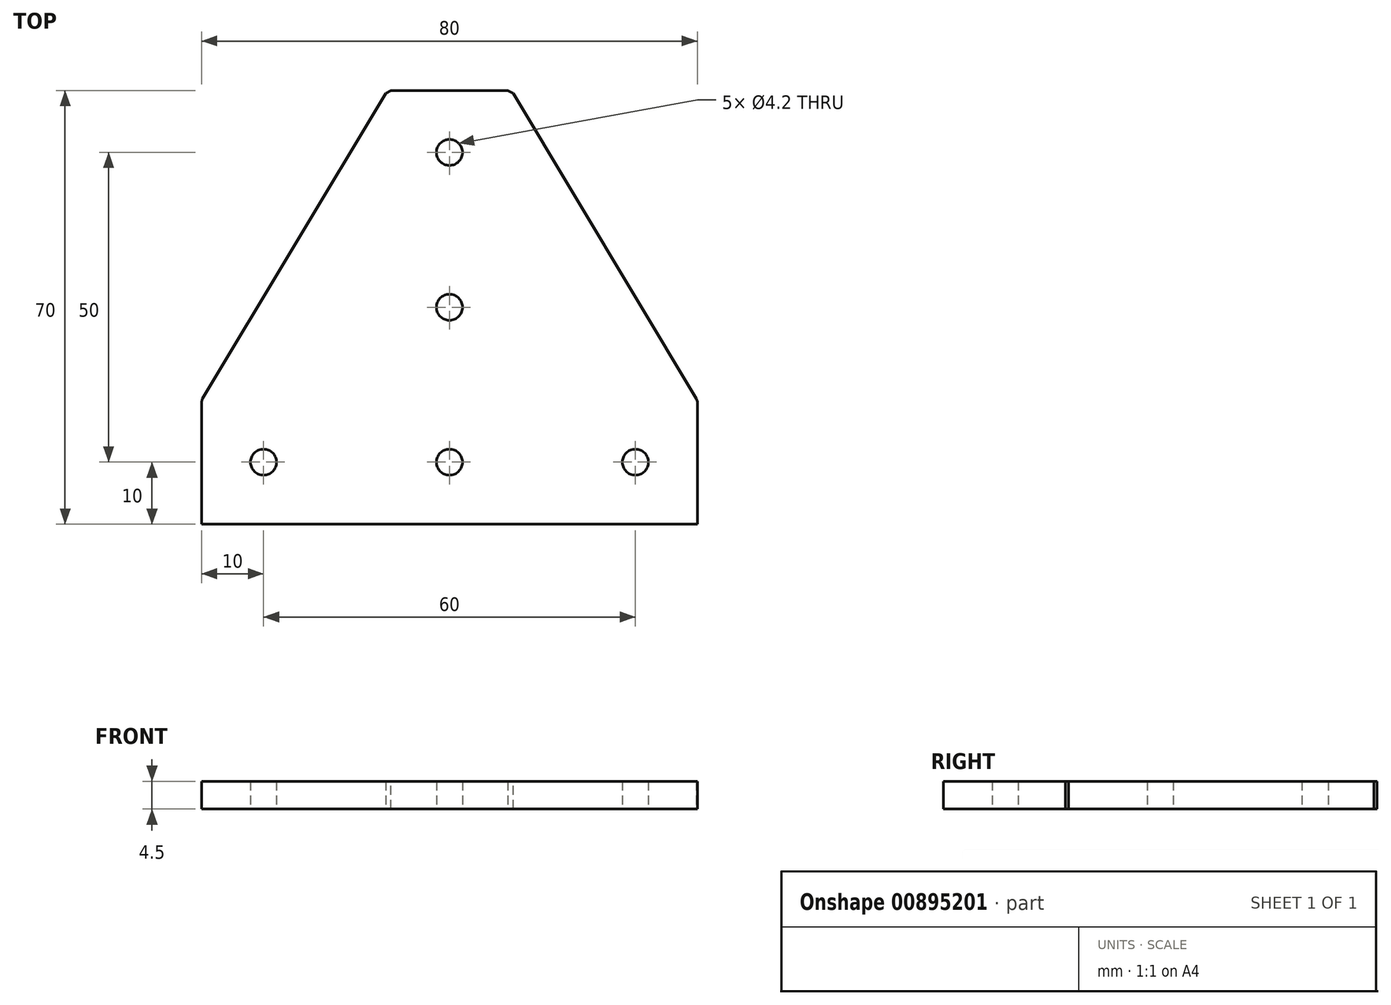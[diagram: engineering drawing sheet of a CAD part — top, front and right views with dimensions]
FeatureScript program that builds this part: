
annotation { "Feature Type Name" : "Feature", "Feature Type Description" : "" }
export const myFeature = defineFeature(function(context is Context, id is Id, definition is map)
    precondition{}
    {
        {
            var Q0;
            Q0=qCreatedBy(makeId("Top.planeOp"),FACE);
            var sketch = newSketch(context, id + "F0", { "sketchPlane" : qUnion([Q0])});
            skLineSegment(sketch, "E0", {"start": v(0, 0) * mm, "end": v(40, 0) * mm});
            skLineSegment(sketch, "E1", {"start": v(40, 0) * mm, "end": v(40, 20) * mm});
            skLineSegment(sketch, "E2.0", {"start": v(0, 60) * mm, "end": v(40, 60) * mm, "construction": true});
            skLineSegment(sketch, "E3", {"start": v(0, 60) * mm, "end": v(0, -24.18) * mm, "construction": true});
            skLineSegment(sketch, "E4.0", {"start": v(-10, 60) * mm, "end": v(-10, -24.18) * mm, "construction": true});
            skLineSegment(sketch, "E5.0", {"start": v(10, 70) * mm, "end": v(10, -24.18) * mm, "construction": true});
            skLineSegment(sketch, "E6.MirrorCS", {"start": v(0, 60) * mm, "end": v(-40, 60) * mm});
            skLineSegment(sketch, "E7.MirrorCS", {"start": v(-40, 0) * mm, "end": v(-40, 20) * mm});
            skLineSegment(sketch, "E8.MirrorCS", {"start": v(0, 0) * mm, "end": v(-40, 0) * mm});
            skLineSegment(sketch, "E9.0", {"start": v(40, 10) * mm, "end": v(-40, 10) * mm, "construction": true});
            skLineSegment(sketch, "E10.0", {"start": v(0, 70) * mm, "end": v(10, 70) * mm});
            skLineSegment(sketch, "E11.MirrorCS", {"start": v(-10, 70) * mm, "end": v(-10, -24.18) * mm, "construction": true});
            skLineSegment(sketch, "E12.MirrorCS", {"start": v(0, 70) * mm, "end": v(-10, 70) * mm});
            skLineSegment(sketch, "E13", {"start": v(-10, 70) * mm, "end": v(-40, 20) * mm});
            skLineSegment(sketch, "E14", {"start": v(10, 70) * mm, "end": v(40, 20) * mm});
            skPoint(sketch, "E15.orphan", {"position": v(40, 70) * mm});
            skPoint(sketch, "E16.orphan", {"position": v(-40, 70) * mm});
            skLineSegment(sketch, "E17.0", {"start": v(-30, 60) * mm, "end": v(-30, -24.18) * mm, "construction": true});
            skLineSegment(sketch, "E18.0", {"start": v(30, 60) * mm, "end": v(30, -24.18) * mm, "construction": true});
            skLineSegment(sketch, "E19.0", {"start": v(40, 35) * mm, "end": v(-40, 35) * mm, "construction": true});
            skLineSegment(sketch, "E20.0", {"start": v(40, 60) * mm, "end": v(-40, 60) * mm, "construction": true});
            skCircle(sketch, "E21", {"center": v(0, 60) * mm, "radius": 2.1 * mm});
            skCircle(sketch, "E22", {"center": v(0, 35) * mm, "radius": 2.1 * mm});
            skCircle(sketch, "E23", {"center": v(0, 10) * mm, "radius": 2.1 * mm});
            skCircle(sketch, "E24", {"center": v(-30, 10) * mm, "radius": 2.1 * mm});
            skCircle(sketch, "E25", {"center": v(30, 10) * mm, "radius": 2.1 * mm});
            skSolve(sketch);
        }
        {
            var Q0;
            Q0=makeQuery(id+"F0.imprint","IMPRINT",FACE,{"disambiguationData":[TD([[makeQuery(id+"F0.imprint","IMPRINT",EDGE,{"derivedFrom":sQuery(id+"F0.wireOp",EDGE,"E0")}),1.0]])]});
            extrude(context, id + "F1", {"entities" : qUnion([Q0]), "depth" : 4.5 * mm, "offsetDistance" : 25 * mm});
        }
        {
            var Q0;
            Q0=makeQuery(id+"F1.opExtrude","SWEPT_EDGE",EDGE,{"disambiguationData":[OSD([sQuery(id+"F0.wireOp",EDGE,"E12.MirrorCS"),sQuery(id+"F0.wireOp",EDGE,"E13")])]});
            var Q1;
            Q1=makeQuery(id+"F1.opExtrude","SWEPT_EDGE",EDGE,{"disambiguationData":[OSD([sQuery(id+"F0.wireOp",EDGE,"E10.0"),sQuery(id+"F0.wireOp",EDGE,"E14")])]});
            var Q2;
            Q2=makeQuery(id+"F1.opExtrude","SWEPT_EDGE",EDGE,{"disambiguationData":[OSD([sQuery(id+"F0.wireOp",EDGE,"E1"),sQuery(id+"F0.wireOp",EDGE,"E14")])]});
            var Q3;
            Q3=makeQuery(id+"F1.opExtrude","SWEPT_EDGE",EDGE,{"disambiguationData":[OSD([sQuery(id+"F0.wireOp",EDGE,"E7.MirrorCS"),sQuery(id+"F0.wireOp",EDGE,"E13")])]});
            chamfer(context, id + "F2", {"entities" : qUnion([Q0, Q1, Q2, Q3]), "width" : 1 * mm, "tangentPropagation" : true});
        }
    });
